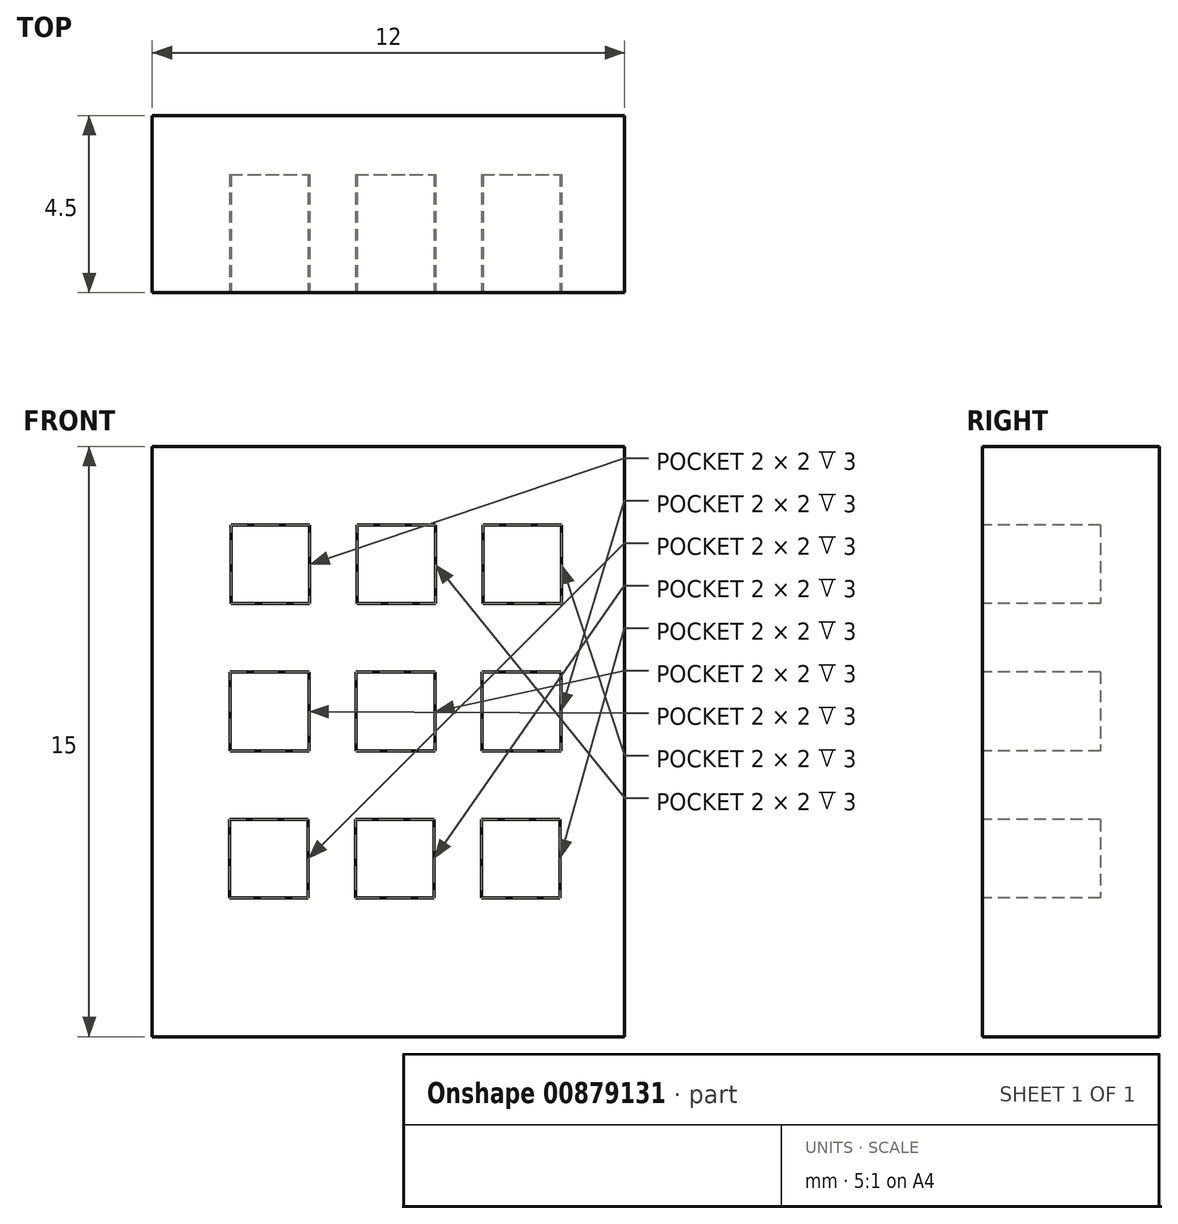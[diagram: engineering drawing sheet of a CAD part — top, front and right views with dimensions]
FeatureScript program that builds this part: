
annotation { "Feature Type Name" : "Feature", "Feature Type Description" : "" }
export const myFeature = defineFeature(function(context is Context, id is Id, definition is map)
    precondition{}
    {
        {
            var Q0;
            Q0=qCreatedBy(makeId("Top.planeOp"),FACE);
            var sketch = newSketch(context, id + "F0", { "sketchPlane" : qUnion([Q0])});
            skLineSegment(sketch, "E0.bottom", {"start": v(0, 0) * mm, "end": v(12, 0) * mm});
            skLineSegment(sketch, "E0.top", {"start": v(0, 4.5) * mm, "end": v(12, 4.5) * mm});
            skLineSegment(sketch, "E0.left", {"start": v(0, 0) * mm, "end": v(0, 4.5) * mm});
            skLineSegment(sketch, "E0.right", {"start": v(12, 0) * mm, "end": v(12, 4.5) * mm});
            skSolve(sketch);
        }
        {
            var Q0;
            Q0 = qSketchRegion(id + "F0", true);
            extrude(context, id + "F1", {"entities" : qUnion([Q0]), "depth" : 15 * mm, "offsetDistance" : 25 * mm});
        }
        {
            var Q0;
            Q0=makeQuery(id+"F1.opExtrude","SWEPT_FACE",FACE,{"disambiguationData":[OSD([sQuery(id+"F0.wireOp",EDGE,"E0.bottom")])]});
            var sketch = newSketch(context, id + "F2", { "sketchPlane" : qUnion([Q0])});
            skLineSegment(sketch, "E1.bottom", {"start": v(2, 13) * mm, "end": v(4, 13) * mm});
            skLineSegment(sketch, "E1.top", {"start": v(2, 11) * mm, "end": v(4, 11) * mm});
            skLineSegment(sketch, "E1.left", {"start": v(2, 13) * mm, "end": v(2, 11) * mm});
            skLineSegment(sketch, "E1.right", {"start": v(4, 13) * mm, "end": v(4, 11) * mm});
            skLineSegment(sketch, "E2.1.0.0", {"start": v(5.2, 13) * mm, "end": v(5.2, 11) * mm});
            skLineSegment(sketch, "E2.1.0.1", {"start": v(5.2, 11) * mm, "end": v(7.2, 11) * mm});
            skLineSegment(sketch, "E2.1.0.2", {"start": v(7.2, 13) * mm, "end": v(7.2, 11) * mm});
            skLineSegment(sketch, "E2.1.0.3", {"start": v(5.2, 13) * mm, "end": v(7.2, 13) * mm});
            skLineSegment(sketch, "E2.2.0.0", {"start": v(8.4, 13) * mm, "end": v(8.4, 11) * mm});
            skLineSegment(sketch, "E2.2.0.1", {"start": v(8.4, 11) * mm, "end": v(10.4, 11) * mm});
            skLineSegment(sketch, "E2.2.0.2", {"start": v(10.4, 13) * mm, "end": v(10.4, 11) * mm});
            skLineSegment(sketch, "E2.2.0.3", {"start": v(8.4, 13) * mm, "end": v(10.4, 13) * mm});
            skLineSegment(sketch, "E2.direction1", {"start": v(2, 11) * mm, "end": v(5.2, 11) * mm, "construction": true});
            skLineSegment(sketch, "E3.1.0.1", {"start": v(3.98, 9.26) * mm, "end": v(3.98, 7.26) * mm});
            skLineSegment(sketch, "E3.1.0.2", {"start": v(1.98, 9.26) * mm, "end": v(3.98, 9.26) * mm});
            skLineSegment(sketch, "E3.1.0.3", {"start": v(1.98, 9.26) * mm, "end": v(1.98, 7.26) * mm});
            skLineSegment(sketch, "E3.1.0.4", {"start": v(5.18, 9.26) * mm, "end": v(5.18, 7.26) * mm});
            skLineSegment(sketch, "E3.1.0.5", {"start": v(5.18, 9.26) * mm, "end": v(7.18, 9.26) * mm});
            skLineSegment(sketch, "E3.1.0.6", {"start": v(7.18, 9.26) * mm, "end": v(7.18, 7.26) * mm});
            skLineSegment(sketch, "E3.1.0.7", {"start": v(5.18, 7.26) * mm, "end": v(7.18, 7.26) * mm});
            skLineSegment(sketch, "E3.1.0.8", {"start": v(8.38, 7.26) * mm, "end": v(10.38, 7.26) * mm});
            skLineSegment(sketch, "E3.1.0.9", {"start": v(8.38, 9.26) * mm, "end": v(8.38, 7.26) * mm});
            skLineSegment(sketch, "E3.1.0.10", {"start": v(8.38, 9.26) * mm, "end": v(10.38, 9.26) * mm});
            skLineSegment(sketch, "E3.1.0.11", {"start": v(10.38, 9.26) * mm, "end": v(10.38, 7.26) * mm});
            skLineSegment(sketch, "E3.2.0.1", {"start": v(3.96, 5.52) * mm, "end": v(3.96, 3.52) * mm});
            skLineSegment(sketch, "E3.2.0.2", {"start": v(1.96, 5.52) * mm, "end": v(3.96, 5.52) * mm});
            skLineSegment(sketch, "E3.2.0.3", {"start": v(1.96, 5.52) * mm, "end": v(1.96, 3.52) * mm});
            skLineSegment(sketch, "E3.2.0.4", {"start": v(5.16, 5.52) * mm, "end": v(5.16, 3.52) * mm});
            skLineSegment(sketch, "E3.2.0.5", {"start": v(5.16, 5.52) * mm, "end": v(7.16, 5.52) * mm});
            skLineSegment(sketch, "E3.2.0.6", {"start": v(7.16, 5.52) * mm, "end": v(7.16, 3.52) * mm});
            skLineSegment(sketch, "E3.2.0.7", {"start": v(5.16, 3.52) * mm, "end": v(7.16, 3.52) * mm});
            skLineSegment(sketch, "E3.2.0.8", {"start": v(8.36, 3.52) * mm, "end": v(10.36, 3.52) * mm});
            skLineSegment(sketch, "E3.2.0.9", {"start": v(8.36, 5.52) * mm, "end": v(8.36, 3.52) * mm});
            skLineSegment(sketch, "E3.2.0.10", {"start": v(8.36, 5.52) * mm, "end": v(10.36, 5.52) * mm});
            skLineSegment(sketch, "E3.2.0.11", {"start": v(10.36, 5.52) * mm, "end": v(10.36, 3.52) * mm});
            skLineSegment(sketch, "E3.direction1", {"start": v(2, 11) * mm, "end": v(1.98, 7.26) * mm, "construction": true});
            skLineSegment(sketch, "E4", {"start": v(1.98, 7.26) * mm, "end": v(3.98, 7.26) * mm});
            skLineSegment(sketch, "E5", {"start": v(3.96, 3.52) * mm, "end": v(1.96, 3.52) * mm});
            skSolve(sketch);
        }
        {
            var Q0;
            Q0 = qSketchRegion(id + "F2", true);
            extrude(context, id + "F3", {"entities" : qUnion([Q0]), "operationType" : NewBodyOperationType.REMOVE, "oppositeDirection" : true, "depth" : 3 * mm, "offsetDistance" : 25 * mm});
        }
    });
